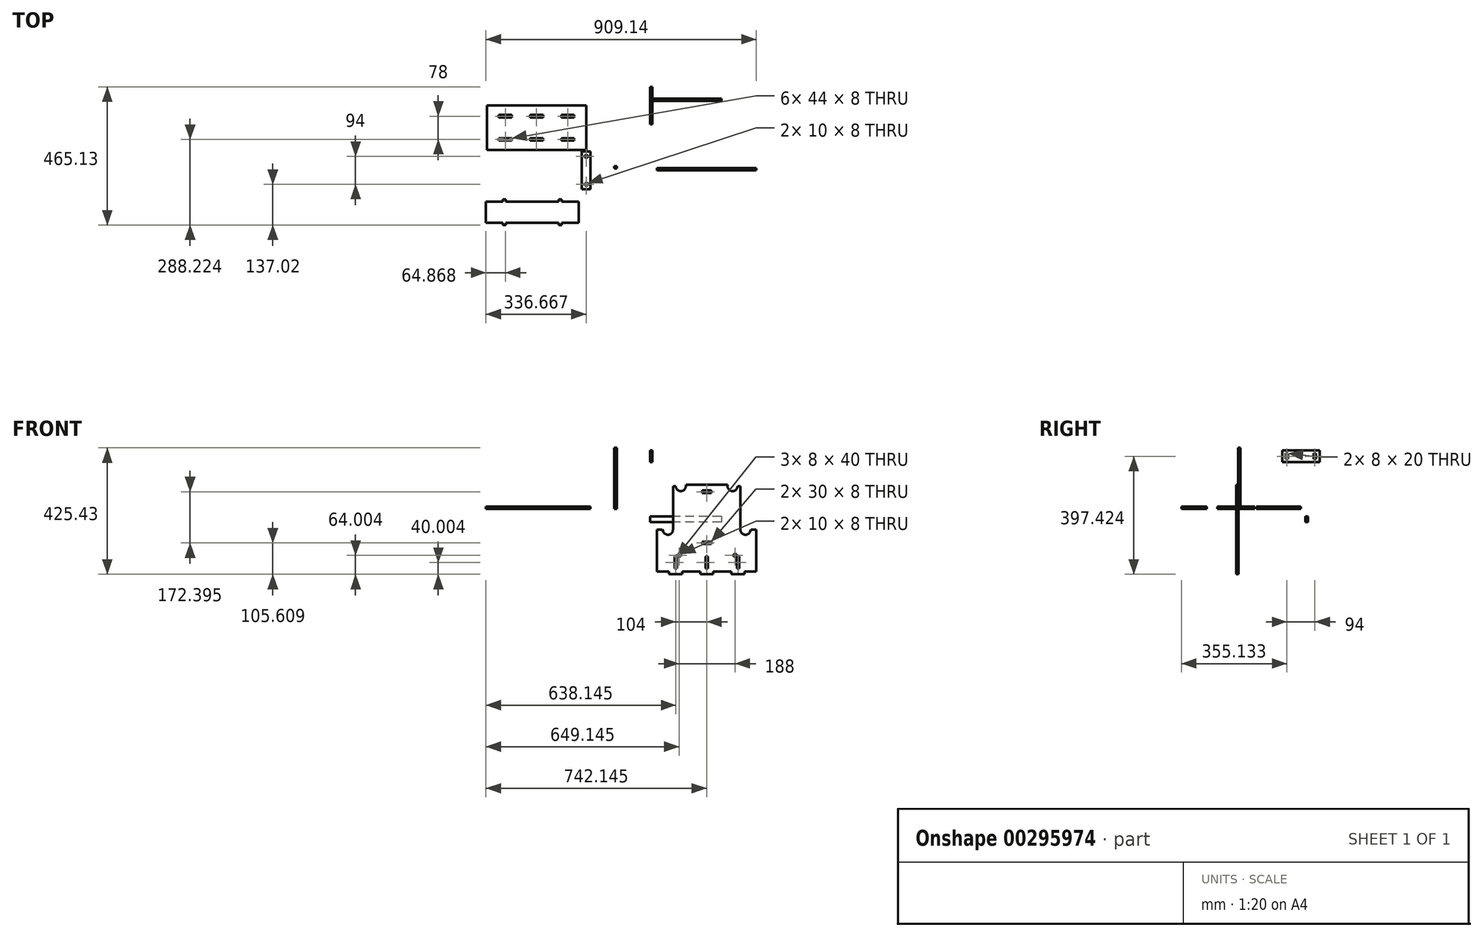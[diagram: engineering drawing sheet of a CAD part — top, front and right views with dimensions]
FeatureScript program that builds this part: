
annotation { "Feature Type Name" : "Feature", "Feature Type Description" : "" }
export const myFeature = defineFeature(function(context is Context, id is Id, definition is map)
    precondition{}
    {
        {
            var Q0;
            Q0=qCreatedBy(makeId("Front.planeOp"),FACE);
            var sketch = newSketch(context, id + "F0", { "sketchPlane" : qUnion([Q0])});
            skLineSegment(sketch, "E0", {"start": v(190.75, -220.43) * mm, "end": v(212.75, -220.43) * mm});
            skLineSegment(sketch, "E1", {"start": v(357.75, -69.41) * mm, "end": v(339.75, -69.41) * mm});
            skLineSegment(sketch, "E2", {"start": v(339.75, -69.41) * mm, "end": v(337.07, -76.47) * mm});
            skLineSegment(sketch, "E3", {"start": v(304.18, -70.43) * mm, "end": v(304.18, 75.95) * mm});
            skLineSegment(sketch, "E4", {"start": v(304.18, 75.95) * mm, "end": v(295.18, 75.95) * mm});
            skLineSegment(sketch, "E5", {"start": v(295.18, 75.95) * mm, "end": v(294.18, 72.2) * mm});
            skLineSegment(sketch, "E6", {"start": v(260.75, 76.57) * mm, "end": v(260.75, 81.57) * mm});
            skLineSegment(sketch, "E7", {"start": v(260.75, 81.57) * mm, "end": v(190.75, 81.57) * mm});
            skArc(sketch, "E8", {"start": v(294.18, 72.2) * mm, "mid": v(275.55, 59.72) * mm, "end": v(260.75, 76.57) * mm});
            skArc(sketch, "E9", {"start": v(304.18, -70.43) * mm, "mid": v(318.1, -87.15) * mm, "end": v(337.07, -76.47) * mm});
            skLineSegment(sketch, "E10.right", {"start": v(205.75, 61.57) * mm, "end": v(205.75, 53.57) * mm});
            skLineSegment(sketch, "E11.bottom", {"start": v(292.75, -160.43) * mm, "end": v(300.75, -160.43) * mm});
            skLineSegment(sketch, "E11.top", {"start": v(292.75, -200.43) * mm, "end": v(300.75, -200.43) * mm});
            skLineSegment(sketch, "E11.right", {"start": v(300.75, -160.43) * mm, "end": v(300.75, -200.43) * mm});
            skLineSegment(sketch, "E12.right", {"start": v(194.75, -160.43) * mm, "end": v(194.75, -200.43) * mm});
            skLineSegment(sketch, "E13.right", {"start": v(205.75, -118.82) * mm, "end": v(205.75, -110.82) * mm});
            skLineSegment(sketch, "E14.MirrorCS", {"start": v(90.75, -200.43) * mm, "end": v(82.75, -200.43) * mm});
            skLineSegment(sketch, "E15.MirrorCS", {"start": v(86.33, 75.95) * mm, "end": v(87.33, 72.2) * mm});
            skLineSegment(sketch, "E16.MirrorCS", {"start": v(175.75, 61.57) * mm, "end": v(175.75, 53.57) * mm});
            skLineSegment(sketch, "E17.MirrorCS", {"start": v(175.75, -118.82) * mm, "end": v(175.75, -110.82) * mm});
            skLineSegment(sketch, "E18.MirrorCS", {"start": v(41.75, -69.41) * mm, "end": v(44.44, -76.47) * mm});
            skLineSegment(sketch, "E19.MirrorCS", {"start": v(194.75, -200.43) * mm, "end": v(186.75, -200.43) * mm});
            skLineSegment(sketch, "E20.MirrorCS", {"start": v(194.75, -160.43) * mm, "end": v(186.75, -160.43) * mm});
            skLineSegment(sketch, "E21.MirrorCS", {"start": v(77.33, 75.95) * mm, "end": v(86.33, 75.95) * mm});
            skLineSegment(sketch, "E22.MirrorCS", {"start": v(90.75, -160.43) * mm, "end": v(82.75, -160.43) * mm});
            skLineSegment(sketch, "E23.MirrorCS", {"start": v(120.75, 76.57) * mm, "end": v(120.75, 81.57) * mm});
            skLineSegment(sketch, "E24.MirrorCS", {"start": v(205.75, 61.57) * mm, "end": v(175.75, 61.57) * mm});
            skLineSegment(sketch, "E25.MirrorCS", {"start": v(23.75, -69.41) * mm, "end": v(41.75, -69.41) * mm});
            skLineSegment(sketch, "E26.MirrorCS", {"start": v(82.75, -160.43) * mm, "end": v(82.75, -200.43) * mm});
            skLineSegment(sketch, "E27.MirrorCS", {"start": v(205.75, -110.82) * mm, "end": v(175.75, -110.82) * mm});
            skLineSegment(sketch, "E28.MirrorCS", {"start": v(186.75, -160.43) * mm, "end": v(186.75, -200.43) * mm});
            skLineSegment(sketch, "E29.MirrorCS", {"start": v(205.75, -118.82) * mm, "end": v(175.75, -118.82) * mm});
            skLineSegment(sketch, "E30.MirrorCS", {"start": v(77.33, -70.43) * mm, "end": v(77.33, 75.95) * mm});
            skArc(sketch, "E31.MirrorCS", {"start": v(77.33, -70.43) * mm, "mid": v(63.4, -87.15) * mm, "end": v(44.44, -76.47) * mm});
            skArc(sketch, "E32.MirrorCS", {"start": v(87.33, 72.2) * mm, "mid": v(105.96, 59.72) * mm, "end": v(120.75, 76.57) * mm});
            skLineSegment(sketch, "E33.MirrorCS", {"start": v(205.75, 53.57) * mm, "end": v(175.75, 53.57) * mm});
            skLineSegment(sketch, "E34.MirrorCS", {"start": v(120.75, 81.57) * mm, "end": v(190.75, 81.57) * mm});
            skLineSegment(sketch, "E35.MirrorCS", {"start": v(190.75, -220.43) * mm, "end": v(168.75, -220.43) * mm});
            skLineSegment(sketch, "E36", {"start": v(90.75, -160.43) * mm, "end": v(90.75, -200.43) * mm});
            skLineSegment(sketch, "E37", {"start": v(292.75, -160.43) * mm, "end": v(292.75, -200.43) * mm});
            skLineSegment(sketch, "E38.top", {"start": v(92.75, -152.43) * mm, "end": v(102.75, -152.43) * mm});
            skLineSegment(sketch, "E38.left", {"start": v(92.75, -160.43) * mm, "end": v(92.75, -152.43) * mm});
            skLineSegment(sketch, "E38.right", {"start": v(102.75, -160.43) * mm, "end": v(102.75, -152.43) * mm});
            skLineSegment(sketch, "E39", {"start": v(92.75, -160.43) * mm, "end": v(102.75, -160.43) * mm});
            skLineSegment(sketch, "E40.bottom", {"start": v(290.75, -160.43) * mm, "end": v(280.75, -160.43) * mm});
            skLineSegment(sketch, "E40.top", {"start": v(290.75, -152.43) * mm, "end": v(280.75, -152.43) * mm});
            skLineSegment(sketch, "E40.left", {"start": v(290.75, -160.43) * mm, "end": v(290.75, -152.43) * mm});
            skLineSegment(sketch, "E40.right", {"start": v(280.75, -160.43) * mm, "end": v(280.75, -152.43) * mm});
            skLineSegment(sketch, "E41", {"start": v(23.75, -210.93) * mm, "end": v(63.75, -210.93) * mm});
            skLineSegment(sketch, "E42", {"start": v(63.75, -210.93) * mm, "end": v(63.75, -220.43) * mm});
            skLineSegment(sketch, "E43", {"start": v(23.75, -210.93) * mm, "end": v(23.75, -69.41) * mm});
            skLineSegment(sketch, "E44", {"start": v(357.75, -210.93) * mm, "end": v(317.75, -210.93) * mm});
            skLineSegment(sketch, "E45", {"start": v(317.75, -210.93) * mm, "end": v(317.75, -220.43) * mm});
            skLineSegment(sketch, "E46", {"start": v(107.75, -220.43) * mm, "end": v(107.75, -210.93) * mm});
            skLineSegment(sketch, "E47", {"start": v(107.75, -210.93) * mm, "end": v(168.75, -210.93) * mm});
            skLineSegment(sketch, "E48", {"start": v(168.75, -210.93) * mm, "end": v(168.75, -220.43) * mm});
            skLineSegment(sketch, "E49", {"start": v(273.75, -220.43) * mm, "end": v(273.75, -210.93) * mm});
            skLineSegment(sketch, "E50", {"start": v(273.75, -210.93) * mm, "end": v(212.75, -210.93) * mm});
            skLineSegment(sketch, "E51", {"start": v(212.75, -210.93) * mm, "end": v(212.75, -220.43) * mm});
            skLineSegment(sketch, "E52", {"start": v(107.75, -220.43) * mm, "end": v(63.75, -220.43) * mm});
            skLineSegment(sketch, "E53", {"start": v(273.75, -220.43) * mm, "end": v(317.75, -220.43) * mm});
            skLineSegment(sketch, "E54", {"start": v(357.75, -210.93) * mm, "end": v(357.75, -69.41) * mm});
            skSolve(sketch);
        }
        {
            var Q0;
            Q0 = qSketchRegion(id + "F0", true);
            extrude(context, id + "F1", {"entities" : qUnion([Q0]), "depth" : 8 * mm});
        }
        {
            var Q0;
            Q0=qCreatedBy(makeId("Top.planeOp"),FACE);
            var sketch = newSketch(context, id + "F2", { "sketchPlane" : qUnion([Q0])});
            skLineSegment(sketch, "E55.bottom", {"start": v(-229.72, 54.78) * mm, "end": v(-199.72, 54.78) * mm});
            skLineSegment(sketch, "E55.top", {"start": v(-229.72, -71.22) * mm, "end": v(-199.72, -71.22) * mm});
            skLineSegment(sketch, "E55.left", {"start": v(-229.72, 54.78) * mm, "end": v(-229.72, -71.22) * mm});
            skLineSegment(sketch, "E55.right", {"start": v(-199.72, 54.78) * mm, "end": v(-199.72, -71.22) * mm});
            skLineSegment(sketch, "E56.bottom", {"start": v(-219.72, 42.78) * mm, "end": v(-209.72, 42.78) * mm});
            skLineSegment(sketch, "E56.top", {"start": v(-219.72, 34.78) * mm, "end": v(-209.72, 34.78) * mm});
            skLineSegment(sketch, "E56.left", {"start": v(-219.72, 42.78) * mm, "end": v(-219.72, 34.78) * mm});
            skLineSegment(sketch, "E56.right", {"start": v(-209.72, 42.78) * mm, "end": v(-209.72, 34.78) * mm});
            skLineSegment(sketch, "E57.bottom", {"start": v(-219.72, -59.22) * mm, "end": v(-209.72, -59.22) * mm});
            skLineSegment(sketch, "E57.top", {"start": v(-219.72, -51.22) * mm, "end": v(-209.72, -51.22) * mm});
            skLineSegment(sketch, "E57.left", {"start": v(-219.72, -59.22) * mm, "end": v(-219.72, -51.22) * mm});
            skLineSegment(sketch, "E57.right", {"start": v(-209.72, -59.22) * mm, "end": v(-209.72, -51.22) * mm});
            skSolve(sketch);
        }
        {
            var Q0;
            Q0=makeQuery(id+"F2.imprint","IMPRINT",FACE,{"disambiguationData":[TD([[makeQuery(id+"F2.imprint","IMPRINT",EDGE,{"derivedFrom":sQuery(id+"F2.wireOp",EDGE,"E55.bottom")}),-1.0]])]});
            extrude(context, id + "F3", {"entities" : qUnion([Q0]), "depth" : 8 * mm});
        }
        {
            var Q0;
            Q0=qCreatedBy(makeId("Right.planeOp"),FACE);
            var sketch = newSketch(context, id + "F4", { "sketchPlane" : qUnion([Q0])});
            skLineSegment(sketch, "E58.bottom", {"start": v(272.9, 197) * mm, "end": v(146.9, 197) * mm});
            skLineSegment(sketch, "E58.top", {"start": v(272.9, 157) * mm, "end": v(146.9, 157) * mm});
            skLineSegment(sketch, "E58.left", {"start": v(272.9, 197) * mm, "end": v(272.9, 157) * mm});
            skLineSegment(sketch, "E58.right", {"start": v(146.9, 197) * mm, "end": v(146.9, 157) * mm});
            skLineSegment(sketch, "E59.bottom", {"start": v(166.9, 167) * mm, "end": v(158.9, 167) * mm});
            skLineSegment(sketch, "E59.top", {"start": v(166.9, 187) * mm, "end": v(158.9, 187) * mm});
            skLineSegment(sketch, "E59.left", {"start": v(166.9, 167) * mm, "end": v(166.9, 187) * mm});
            skLineSegment(sketch, "E59.right", {"start": v(158.9, 167) * mm, "end": v(158.9, 187) * mm});
            skLineSegment(sketch, "E60.bottom", {"start": v(260.9, 187) * mm, "end": v(252.9, 187) * mm});
            skLineSegment(sketch, "E60.top", {"start": v(260.9, 167) * mm, "end": v(252.9, 167) * mm});
            skLineSegment(sketch, "E60.left", {"start": v(260.9, 187) * mm, "end": v(260.9, 167) * mm});
            skLineSegment(sketch, "E60.right", {"start": v(252.9, 187) * mm, "end": v(252.9, 167) * mm});
            skSolve(sketch);
        }
        {
            var Q0;
            Q0 = qSketchRegion(id + "F4", true);
            extrude(context, id + "F5", {"entities" : qUnion([Q0]), "depth" : 8 * mm});
        }
        {
            var Q0;
            Q0=qCreatedBy(makeId("Right.planeOp"),FACE);
            var sketch = newSketch(context, id + "F6", { "sketchPlane" : qUnion([Q0])});
            skLineSegment(sketch, "E61.bottom", {"start": v(233.2, -25.13) * mm, "end": v(225.2, -25.13) * mm});
            skLineSegment(sketch, "E61.top", {"start": v(233.2, -45.13) * mm, "end": v(225.2, -45.13) * mm});
            skLineSegment(sketch, "E61.left", {"start": v(233.2, -25.13) * mm, "end": v(233.2, -45.13) * mm});
            skLineSegment(sketch, "E61.right", {"start": v(225.2, -25.13) * mm, "end": v(225.2, -45.13) * mm});
            skSolve(sketch);
        }
        {
            var Q0;
            Q0 = qSketchRegion(id + "F6", true);
            extrude(context, id + "F7", {"entities" : qUnion([Q0]), "depth" : 240 * mm});
        }
        {
            var Q0;
            Q0=qCreatedBy(makeId("Top.planeOp"),FACE);
            var sketch = newSketch(context, id + "F8", { "sketchPlane" : qUnion([Q0])});
            skLineSegment(sketch, "E62.bottom", {"start": v(-120.78, 6.37) * mm, "end": v(-110.78, 6.37) * mm});
            skLineSegment(sketch, "E62.top", {"start": v(-120.78, -1.63) * mm, "end": v(-110.78, -1.63) * mm});
            skLineSegment(sketch, "E62.left", {"start": v(-120.78, 6.37) * mm, "end": v(-120.78, -1.63) * mm});
            skLineSegment(sketch, "E62.right", {"start": v(-110.78, 6.37) * mm, "end": v(-110.78, -1.63) * mm});
            skSolve(sketch);
        }
        {
            var Q0;
            Q0 = qSketchRegion(id + "F8", true);
            extrude(context, id + "F9", {"entities" : qUnion([Q0]), "depth" : 205 * mm});
        }
        {
            var Q0;
            Q0=qCreatedBy(makeId("Top.planeOp"),FACE);
            var sketch = newSketch(context, id + "F10", { "sketchPlane" : qUnion([Q0])});
            skLineSegment(sketch, "E63", {"start": v(-551.39, -114.24) * mm, "end": v(-551.39, -184.24) * mm});
            skLineSegment(sketch, "E64", {"start": v(-551.39, -184.24) * mm, "end": v(-494.39, -184.24) * mm});
            skLineSegment(sketch, "E65", {"start": v(-494.39, -184.24) * mm, "end": v(-494.39, -192.24) * mm});
            skLineSegment(sketch, "E66", {"start": v(-494.39, -192.24) * mm, "end": v(-484.39, -192.24) * mm});
            skLineSegment(sketch, "E67", {"start": v(-484.39, -192.24) * mm, "end": v(-484.39, -184.24) * mm});
            skLineSegment(sketch, "E68", {"start": v(-484.39, -184.24) * mm, "end": v(-395.39, -184.24) * mm});
            skLineSegment(sketch, "E69", {"start": v(-395.39, -184.24) * mm, "end": v(-395.39, -114.24) * mm});
            skLineSegment(sketch, "E70", {"start": v(-395.39, -114.24) * mm, "end": v(-484.39, -114.24) * mm});
            skLineSegment(sketch, "E71", {"start": v(-484.39, -114.24) * mm, "end": v(-484.39, -106.24) * mm});
            skLineSegment(sketch, "E72", {"start": v(-484.39, -106.24) * mm, "end": v(-494.39, -106.24) * mm});
            skLineSegment(sketch, "E73", {"start": v(-494.39, -106.24) * mm, "end": v(-494.39, -114.24) * mm});
            skLineSegment(sketch, "E74", {"start": v(-494.39, -114.24) * mm, "end": v(-551.39, -114.24) * mm});
            skLineSegment(sketch, "E75.MirrorCS", {"start": v(-296.39, -192.24) * mm, "end": v(-306.39, -192.24) * mm});
            skLineSegment(sketch, "E76.MirrorCS", {"start": v(-296.39, -184.24) * mm, "end": v(-296.39, -192.24) * mm});
            skLineSegment(sketch, "E77.MirrorCS", {"start": v(-306.39, -192.24) * mm, "end": v(-306.39, -184.24) * mm});
            skLineSegment(sketch, "E78.MirrorCS", {"start": v(-306.39, -184.24) * mm, "end": v(-395.39, -184.24) * mm});
            skLineSegment(sketch, "E79.MirrorCS", {"start": v(-306.39, -114.24) * mm, "end": v(-306.39, -106.24) * mm});
            skLineSegment(sketch, "E80.MirrorCS", {"start": v(-395.39, -114.24) * mm, "end": v(-306.39, -114.24) * mm});
            skLineSegment(sketch, "E81.MirrorCS", {"start": v(-239.39, -184.24) * mm, "end": v(-296.39, -184.24) * mm});
            skLineSegment(sketch, "E82.MirrorCS", {"start": v(-296.39, -114.24) * mm, "end": v(-239.39, -114.24) * mm});
            skLineSegment(sketch, "E83.MirrorCS", {"start": v(-306.39, -106.24) * mm, "end": v(-296.39, -106.24) * mm});
            skLineSegment(sketch, "E84.MirrorCS", {"start": v(-239.39, -114.24) * mm, "end": v(-239.39, -184.24) * mm});
            skLineSegment(sketch, "E85.MirrorCS", {"start": v(-296.39, -106.24) * mm, "end": v(-296.39, -114.24) * mm});
            skSolve(sketch);
        }
        {
            var Q0;
            Q0 = qSketchRegion(id + "F10", true);
            extrude(context, id + "F11", {"entities" : qUnion([Q0]), "depth" : 8 * mm});
        }
        {
            var Q0;
            Q0=qCreatedBy(makeId("Top.planeOp"),FACE);
            var sketch = newSketch(context, id + "F12", { "sketchPlane" : qUnion([Q0])});
            skLineSegment(sketch, "E86.bottom", {"start": v(-548.52, 134.98) * mm, "end": v(-214.52, 134.98) * mm});
            skLineSegment(sketch, "E86.top", {"start": v(-548.52, 59.98) * mm, "end": v(-214.52, 59.98) * mm});
            skLineSegment(sketch, "E86.left", {"start": v(-548.52, 134.98) * mm, "end": v(-548.52, 59.98) * mm});
            skLineSegment(sketch, "E86.right", {"start": v(-214.52, 134.98) * mm, "end": v(-214.52, 59.98) * mm});
            skLineSegment(sketch, "E87.bottom", {"start": v(-508.52, 99.98) * mm, "end": v(-464.52, 99.98) * mm});
            skLineSegment(sketch, "E87.top", {"start": v(-508.52, 91.98) * mm, "end": v(-464.52, 91.98) * mm});
            skLineSegment(sketch, "E87.left", {"start": v(-508.52, 99.98) * mm, "end": v(-508.52, 91.98) * mm});
            skLineSegment(sketch, "E87.right", {"start": v(-464.52, 99.98) * mm, "end": v(-464.52, 91.98) * mm});
            skLineSegment(sketch, "E88.bottom", {"start": v(-403.52, 99.98) * mm, "end": v(-359.52, 99.98) * mm});
            skLineSegment(sketch, "E88.top", {"start": v(-403.52, 91.98) * mm, "end": v(-359.52, 91.98) * mm});
            skLineSegment(sketch, "E88.left", {"start": v(-403.52, 99.98) * mm, "end": v(-403.52, 91.98) * mm});
            skLineSegment(sketch, "E88.right", {"start": v(-359.52, 99.98) * mm, "end": v(-359.52, 91.98) * mm});
            skLineSegment(sketch, "E89.bottom", {"start": v(-298.52, 99.98) * mm, "end": v(-254.52, 99.98) * mm});
            skLineSegment(sketch, "E89.top", {"start": v(-298.52, 91.98) * mm, "end": v(-254.52, 91.98) * mm});
            skLineSegment(sketch, "E89.left", {"start": v(-298.52, 99.98) * mm, "end": v(-298.52, 91.98) * mm});
            skLineSegment(sketch, "E89.right", {"start": v(-254.52, 99.98) * mm, "end": v(-254.52, 91.98) * mm});
            skLineSegment(sketch, "E90.MirrorCS", {"start": v(-298.52, 169.98) * mm, "end": v(-298.52, 177.98) * mm});
            skLineSegment(sketch, "E91.MirrorCS", {"start": v(-403.52, 177.98) * mm, "end": v(-359.52, 177.98) * mm});
            skLineSegment(sketch, "E92.MirrorCS", {"start": v(-298.52, 169.98) * mm, "end": v(-254.52, 169.98) * mm});
            skLineSegment(sketch, "E93.MirrorCS", {"start": v(-298.52, 177.98) * mm, "end": v(-254.52, 177.98) * mm});
            skLineSegment(sketch, "E94.MirrorCS", {"start": v(-508.52, 169.98) * mm, "end": v(-508.52, 177.98) * mm});
            skLineSegment(sketch, "E95.MirrorCS", {"start": v(-403.52, 169.98) * mm, "end": v(-359.52, 169.98) * mm});
            skLineSegment(sketch, "E96.MirrorCS", {"start": v(-508.52, 177.98) * mm, "end": v(-464.52, 177.98) * mm});
            skLineSegment(sketch, "E97.MirrorCS", {"start": v(-403.52, 169.98) * mm, "end": v(-403.52, 177.98) * mm});
            skLineSegment(sketch, "E98.MirrorCS", {"start": v(-254.52, 169.98) * mm, "end": v(-254.52, 177.98) * mm});
            skLineSegment(sketch, "E99.MirrorCS", {"start": v(-548.52, 209.98) * mm, "end": v(-214.52, 209.98) * mm});
            skLineSegment(sketch, "E100.MirrorCS", {"start": v(-548.52, 134.98) * mm, "end": v(-548.52, 209.98) * mm});
            skLineSegment(sketch, "E101.MirrorCS", {"start": v(-214.52, 134.98) * mm, "end": v(-214.52, 209.98) * mm});
            skLineSegment(sketch, "E102.MirrorCS", {"start": v(-359.52, 169.98) * mm, "end": v(-359.52, 177.98) * mm});
            skLineSegment(sketch, "E103.MirrorCS", {"start": v(-464.52, 169.98) * mm, "end": v(-464.52, 177.98) * mm});
            skLineSegment(sketch, "E104.MirrorCS", {"start": v(-508.52, 169.98) * mm, "end": v(-464.52, 169.98) * mm});
            skSolve(sketch);
        }
        {
            var Q0;
            Q0 = qSketchRegion(id + "F12", true);
            extrude(context, id + "F13", {"entities" : qUnion([Q0]), "depth" : 8 * mm});
        }
    });
